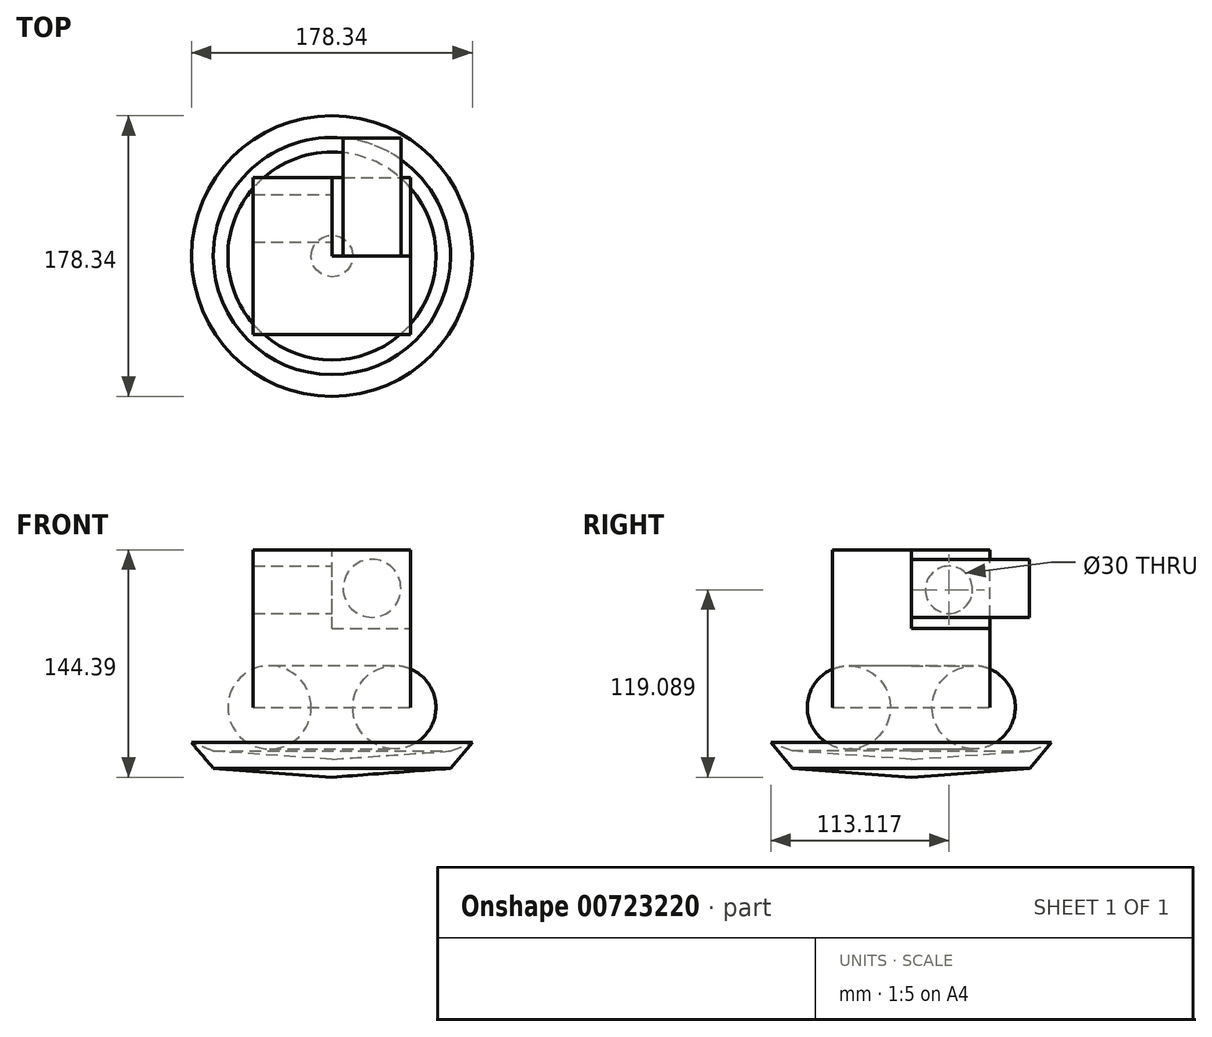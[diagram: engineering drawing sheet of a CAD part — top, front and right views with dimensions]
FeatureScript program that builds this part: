
annotation { "Feature Type Name" : "Feature", "Feature Type Description" : "" }
export const myFeature = defineFeature(function(context is Context, id is Id, definition is map)
    precondition{}
    {
        {
            var Q0;
            Q0=qCreatedBy(makeId("Top.planeOp"),FACE);
            var sketch = newSketch(context, id + "F0", { "sketchPlane" : qUnion([Q0])});
            skLineSegment(sketch, "E0.bottom", {"start": v(-50, -50) * mm, "end": v(50, -50) * mm});
            skLineSegment(sketch, "E0.top", {"start": v(-50, 50) * mm, "end": v(50, 50) * mm});
            skLineSegment(sketch, "E0.left", {"start": v(-50, -50) * mm, "end": v(-50, 50) * mm});
            skLineSegment(sketch, "E0.right", {"start": v(50, -50) * mm, "end": v(50, 50) * mm});
            skPoint(sketch, "E0.middle", {"position": v(0, 0) * mm});
            skSolve(sketch);
        }
        {
            var Q0;
            Q0 = qSketchRegion(id + "F0", true);
            extrude(context, id + "F1", {"entities" : qUnion([Q0]), "depth" : 100 * mm, "offsetDistance" : 25 * mm});
        }
        {
            var Q0;
            Q0=makeQuery(id+"F1.opExtrude","CAP_FACE",FACE,{"disambiguationData":[OSD([sQuery(id+"F0.wireOp",EDGE,"E0.bottom"),sQuery(id+"F0.wireOp",EDGE,"E0.top"),sQuery(id+"F0.wireOp",EDGE,"E0.left"),sQuery(id+"F0.wireOp",EDGE,"E0.right")])],"isStart":false});
            var sketch = newSketch(context, id + "F2", { "sketchPlane" : qUnion([Q0])});
            skLineSegment(sketch, "E1.bottom", {"start": v(0, 0) * mm, "end": v(100, 0) * mm});
            skLineSegment(sketch, "E1.top", {"start": v(0, 100) * mm, "end": v(100, 100) * mm});
            skLineSegment(sketch, "E1.left", {"start": v(0, 0) * mm, "end": v(0, 100) * mm});
            skLineSegment(sketch, "E1.right", {"start": v(100, 0) * mm, "end": v(100, 100) * mm});
            skPoint(sketch, "E1.middle", {"position": v(50, 50) * mm});
            skSolve(sketch);
        }
        {
            var Q0;
            Q0 = qSketchRegion(id + "F2", true);
            extrude(context, id + "F3", {"entities" : qUnion([Q0]), "operationType" : NewBodyOperationType.REMOVE, "depth" : 50 * mm, "offsetDistance" : 25 * mm, "hasSecondDirection" : true, "secondDirectionOppositeDirection" : true, "secondDirectionDepth" : 50 * mm});
        }
        {
            var Q0;
            Q0=makeQuery(id+"F3.boolean.opBoolean","COPY",FACE,{"derivedFrom":makeQuery(id+"F3.opExtrude","SWEPT_FACE",FACE,{"disambiguationData":[OSD([sQuery(id+"F2.wireOp",EDGE,"E1.left")])]})});
            var sketch = newSketch(context, id + "F4", { "sketchPlane" : qUnion([Q0])});
            skCircle(sketch, "E2", {"center": v(23.95, 74.7) * mm, "radius": 15 * mm});
            skSolve(sketch);
        }
        {
            var Q0;
            Q0=makeQuery(id+"F4.imprint","IMPRINT",FACE,{"disambiguationData":[TD([[makeQuery(id+"F4.imprint","IMPRINT",EDGE,{"derivedFrom":sQuery(id+"F4.wireOp",EDGE,"E2")}),1.0]])]});
            extrude(context, id + "F5", {"entities" : qUnion([Q0]), "operationType" : NewBodyOperationType.REMOVE, "oppositeDirection" : true, "depth" : 125 * mm, "offsetDistance" : 25 * mm});
        }
        {
            var Q0;
            Q0=makeQuery(id+"F3.boolean.opBoolean","COPY",FACE,{"derivedFrom":makeQuery(id+"F3.opExtrude","SWEPT_FACE",FACE,{"disambiguationData":[OSD([sQuery(id+"F2.wireOp",EDGE,"E1.bottom")])]})});
            var sketch = newSketch(context, id + "F6", { "sketchPlane" : qUnion([Q0])});
            skCircle(sketch, "E3", {"center": v(-25.45, 75.6) * mm, "radius": 18.36 * mm});
            skLineSegment(sketch, "E4", {"start": v(0, 75.6) * mm, "end": v(-50, 75.6) * mm, "construction": true});
            skPoint(sketch, "E4.startSnap0", {"position": v(0, 75) * mm});
            skLineSegment(sketch, "E5", {"start": v(-50, 75.6) * mm, "end": v(-25.45, 75.6) * mm, "construction": true});
            skLineSegment(sketch, "E6", {"start": v(-25.45, 100) * mm, "end": v(-25.45, 50) * mm, "construction": true});
            skLineSegment(sketch, "E7", {"start": v(-25.45, 50) * mm, "end": v(-25.45, 75.6) * mm, "construction": true});
            skSolve(sketch);
        }
        {
            var Q0;
            Q0=makeQuery(id+"F6.imprint","IMPRINT",FACE,{"disambiguationData":[TD([[makeQuery(id+"F6.imprint","IMPRINT",EDGE,{"derivedFrom":sQuery(id+"F6.wireOp",EDGE,"E3")}),1.0]])]});
            extrude(context, id + "F7", {"entities" : qUnion([Q0]), "operationType" : NewBodyOperationType.ADD, "depth" : 75 * mm, "offsetDistance" : 25 * mm});
        }
        {
            var Q0;
            Q0=qCreatedBy(makeId("Right.planeOp"),FACE);
            var sketch = newSketch(context, id + "F8", { "sketchPlane" : qUnion([Q0])});
            skLineSegment(sketch, "E8", {"start": v(0, 99.8) * mm, "end": v(0, -99.03) * mm, "construction": true});
            skLineSegment(sketch, "E9", {"start": v(0, -99.03) * mm, "end": v(0, 99.8) * mm, "construction": true});
            skCircle(sketch, "E10", {"center": v(39.65, 0) * mm, "radius": 26.42 * mm});
            skArc(sketch, "E11", {"start": v(9.49, 0) * mm, "mid": v(39.65, -30.16) * mm, "end": v(69.82, 0) * mm});
            skLineSegment(sketch, "E12", {"start": v(0, -33.01) * mm, "end": v(75.35, -27.74) * mm});
            skLineSegment(sketch, "E13", {"start": v(75.35, -27.74) * mm, "end": v(89.17, -22.39) * mm});
            skLineSegment(sketch, "E14", {"start": v(89.17, -22.39) * mm, "end": v(75.35, -38.7) * mm});
            skLineSegment(sketch, "E15", {"start": v(75.35, -38.7) * mm, "end": v(0, -44.4) * mm});
            skLineSegment(sketch, "E16", {"start": v(0, -44.4) * mm, "end": v(0, -33.01) * mm});
            skSolve(sketch);
        }
        {
            var Q0;
            Q0=makeQuery(id+"F8.imprint","IMPRINT",FACE,{"disambiguationData":[TD([[makeQuery(id+"F8.imprint","IMPRINT",EDGE,{"derivedFrom":sQuery(id+"F8.wireOp",EDGE,"E10")}),1.0]])]});
            var Q1;
            Q1=sQuery(id+"F8.wireOp",EDGE,"E9");
            revolve(context, id + "F9", {"surfaceOperationType" : NewSurfaceOperationType.NEW, "entities" : qUnion([Q0]), "axis" : qUnion([Q1]), "revolveType" : RevolveType.FULL});
        }
        {
            var Q0;
            Q0 = qSketchRegion(id + "F8", true);
            var Q1;
            Q1=sQuery(id+"F8.wireOp",EDGE,"E9");
            revolve(context, id + "F10", {"surfaceOperationType" : NewSurfaceOperationType.NEW, "entities" : qUnion([Q0]), "axis" : qUnion([Q1]), "revolveType" : RevolveType.FULL});
        }
    });
